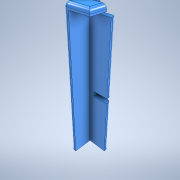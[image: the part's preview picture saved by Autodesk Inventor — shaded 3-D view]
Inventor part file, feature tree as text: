
AUTODESK INVENTOR PART (.ipt)
format: ipt  version: 2021 (Build 250183000, 183)  size: 168,448 bytes
history: native  units: mm
features: extrude x5, sketch x4, fillet x1
ambient origin geometry x8: Origin, YZ Plane, XZ Plane, XY Plane, X Axis, Y Axis, Z Axis, Center Point
bodies: Solid1 (feature_tree)
feature tree (10):
  extrude  "Extrusion1"  Depth=15.0mm
  extrude  "Extrusion3"  Depth=3.0mm
  extrude  "Extrusion4"  Depth=12.0mm
  fillet  "Fillet3"  Radius=3.0mm
  extrude  "Extrusion7"  Depth=12.0mm TaperAngle=0.0deg
  extrude  "Extrusion8"  Depth=2.0mm
  sketch  "Sketch4"  dims[d0=15.0mm d1=15.0mm]
  sketch  "Sketch6"  dims[d2=86.0mm d3=0.0mm d10=3.0mm]
  sketch  "Sketch11"  dims[d11=12.0mm d12=12.0mm d13=3.0mm]
  sketch  "Sketch12"  dims[d14=3.0mm d15=0.0mm d16=12.0mm d17=0.0mm d18=2.0mm d31=6.1mm d32=0.0mm d39=0.0mm d40=0.0mm d49=3.1mm]
